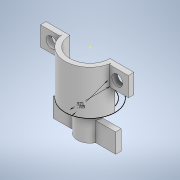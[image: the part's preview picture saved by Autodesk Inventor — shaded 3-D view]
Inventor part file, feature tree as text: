
AUTODESK INVENTOR PART (.ipt)
format: ipt  version: 2020.2 (Build 242310000, 310)  size: 287,744 bytes
history: native  units: in
note: dims shown in document units (in); Inventor stores cm internally (conversion verified against a paired STEP export)
features: sketch x12, extrude x9, hole x2, projected_geometry x2
ambient origin geometry x8: Origin, YZ Plane, XZ Plane, XY Plane, X Axis, Y Axis, Z Axis, Center Point
bodies: Body1 (feature_tree)
feature tree (25):
  extrude  "Extrusion2"  Depth=0.3543in
  extrude  "Extrusion3"  Depth=0.0394in
  extrude  "Extrusion4"  Depth=0.0394in TaperAngle=0.0deg
  sketch  "Sketch11"  dims[d20=0.0394in d59=0.5709in]
  sketch  "Sketch12"  dims[d60=0.7087in d61=0.0787in d62=0.0in]
  extrude  "Extrusion11"  Depth=0.0394in
  extrude  "Extrusion12"  Depth=0.0787in TaperAngle=0.0deg
  sketch  "Sketch14"  dims[d63=0.6299in d64=0.0in d72=0.0039in]
  extrude  "Extrusion14"  Depth=0.6299in
  hole  "Hole1"  [1 undecoded]
  extrude  "Extrusion16"  Depth=0.1575in
  hole  "Hole2"  [1 undecoded]
  extrude  "Extrusion17"  Depth=0.2756in TaperAngle=0.0deg
  extrude  "Extrusion18"  Depth=0.0787in
  sketch  "Sketch3"  dims[d10=0.3543in d11=0.2047in]
  sketch  "Sketch4"  dims[d12=0.1575in d13=0.0in d14=0.0394in]
  projected_geometry  "Projected Loop1"
  sketch  "Sketch5"  dims[d16=0.2362in d17=0.0in d18=0.0394in d19=0.0in]
  sketch  "Sketch15"  dims[d73=0.2756in d74=0.2756in]
  sketch  "Sketch17"  dims[d75=0.2756in d76=0.0in d81=0.1575in]
  sketch  "Sketch18"  dims[d82=0.1575in]
  sketch  "Sketch19"  dims[d83=0.1535in d84=0.75in d85=0.323in d86=0.25in d87=90.0deg d88=1.0in d89=0.8108in d90=0.2756in]
  sketch  "Sketch20"  dims[d91=0.2756in d92=0.2756in d93=0.0in]
  sketch  "Sketch21"  dims[d94=0.1378in d95=0.1378in d96=0.1339in d97=0.75in d98=0.248in d99=0.25in d100=90.0deg d101=1.0in d102=0.8108in d103=5.0in d104=0.0in d105=0.0787in d106=0.0in]
  projected_geometry  "Projected Loop3"
note: 2 required parameter values undecoded (feature->parameter linkage not recoverable at this tier; creation-order binding heuristic only, values carry confidence <= 0.55)
